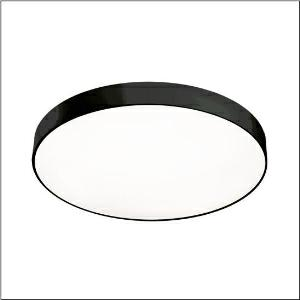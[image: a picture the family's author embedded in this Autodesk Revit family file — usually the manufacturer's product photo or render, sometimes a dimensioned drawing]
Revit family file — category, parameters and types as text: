
# Revit family: round_21_l_51mr38fd0321b
name_source: partatom
category: Lighting Fixtures
units: mm (PartAtom-declared; Revit-internal decimal feet)

## family parameters
Cut with Voids When Loaded = No
Host = Face
Light Source = No
Part Type = Normal
Room Calculation Point = No
Round Connector Dimension = Use Diameter
Shared = No

## types (1)
- Round 21 L (1 x LED, 12490 lm, 98.3 W, 3000K)
    Apparent Load = 98 VA
    CIE Flux Codes = 49 80 96 100 100
    Color Rendering = 80
    Color Temperature = 3000K
    Default Elevation = 1800 mm
    Description = Round 21 L, wall and ceiling luminaire, primary optical cover: cover, of PMMA, opal, light emission: direct distribution, primary light characteristic: symmetric, installation type: suspended mounting, surface-mounted, LED, rated luminous flux: 12.490lm, luminous efficacy: 127lm/W, light colour: 830, colour temperature: 3000K, with terminal, 5-pole, mains connection: 230V, AC, 50/60Hz, rated input power: 98W, housing, of aluminium, coated, black, diameter: 850mm, height: 62mm, protection rating (complete): IP40, insulation class (complete): insulation class I (protective earthing), certification: CE, impact resistance: IK04, permissible operating ambient temperature: -10..+35°C, packaging unit: 1 piece
    Height = 87 mm
    Lamp = 1 x LED
    Lamp Light Flux = 12490 lm
    Lamp Power = 98.3 W
    Lamp count = 1
    Length = 850 mm
    Luminous efficacy = 127 lm/W
    Manufacturer = Siteco
    ModVariant = No
    Model = 51MR38FD0321B
    Mounting Place = Ceiling
    Mounting Type = Surface mounted
    Number of Poles = 1
    OnlyDefault = Yes
    Power Factor = 1
    Product Name = Round 21 L
    Product group = wall and ceiling luminaire
    ProductGroupID = 301
    Protection Class = Protection class I
    Protection Degree = IP 40
    RLX_Detail_Level = 1
    RLX_Emergency_Light_Flux = 0 lm
    RLX_Emergency_Type = 0
    RLX_Emergency_Type_DB = No
    RlxData = <blob elided: 23893 chars, md5=0d1dedf6>
    Socket = socket
    Standby Power = 0 W
    System Light Flux = 12490 lm
    System Power = 98 W
    Type Comments = Product without accessories
    Type Image = l_1258328.jpg
    URL = http://relux.com
    VarID = ---
    Voltage = 0 V
    Weight = 0.00 kg
    Width = 0 mm  [stored 0 ft]

note: [stored X ft] marks values corroborated as IEEE doubles in the binary element streams (Revit-internal decimal feet)

## geometry (parser evidence)
native form markers: Blend x4, Sweep x9
no freeform markers — native parametric forms only
